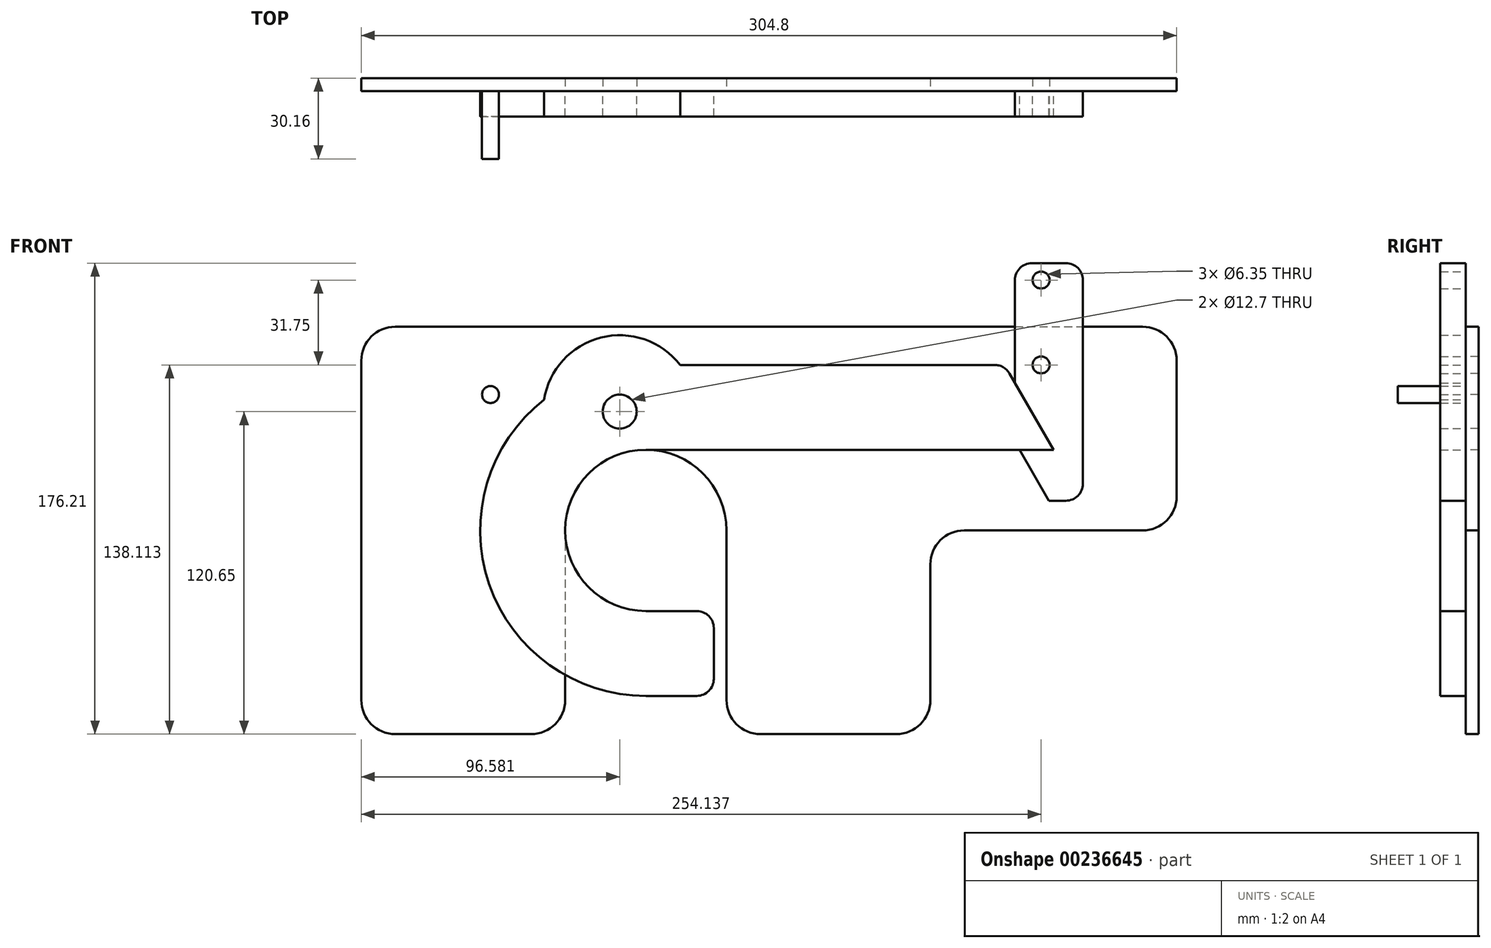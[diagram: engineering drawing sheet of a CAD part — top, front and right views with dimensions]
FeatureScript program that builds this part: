
annotation { "Feature Type Name" : "Feature", "Feature Type Description" : "" }
export const myFeature = defineFeature(function(context is Context, id is Id, definition is map)
    precondition{}
    {
        {
            var Q0;
            Q0=qCreatedBy(makeId("Front.planeOp"),FACE);
            var sketch = newSketch(context, id + "F0", { "sketchPlane" : qUnion([Q0])});
            skArc(sketch, "E0", {"start": v(0, 30.16) * mm, "mid": v(-30.16, 0) * mm, "end": v(0, -30.16) * mm});
            skLineSegment(sketch, "E1", {"start": v(19.05, -61.91) * mm, "end": v(0, -61.91) * mm});
            skLineSegment(sketch, "E2", {"start": v(0, 30.16) * mm, "end": v(152.4, 30.16) * mm});
            skLineSegment(sketch, "E3", {"start": v(0, -30.16) * mm, "end": v(19.05, -30.16) * mm});
            skLineSegment(sketch, "E4", {"start": v(25.4, -36.51) * mm, "end": v(25.4, -55.56) * mm});
            skCircle(sketch, "E5", {"center": v(-9.78, 44.45) * mm, "radius": 6.35 * mm});
            skArc(sketch, "E6", {"start": v(-38, 48.87) * mm, "mid": v(-58.56, -20.1) * mm, "end": v(0, -61.91) * mm});
            skLineSegment(sketch, "E7", {"start": v(12.84, 61.91) * mm, "end": v(130.4, 61.91) * mm});
            skLineSegment(sketch, "E8", {"start": v(152.4, 30.16) * mm, "end": v(135.9, 58.74) * mm});
            skArc(sketch, "E9", {"start": v(12.84, 61.91) * mm, "mid": v(-16.88, 72.13) * mm, "end": v(-38, 48.87) * mm});
            skPoint(sketch, "E10.visualSharp", {"position": v(25.4, -30.16) * mm});
            skArc(sketch, "E10.filletArc", {"start": v(25.4, -36.51) * mm, "mid": v(23.54, -32.02) * mm, "end": v(19.05, -30.16) * mm});
            skPoint(sketch, "E11.visualSharp", {"position": v(25.4, -61.91) * mm});
            skArc(sketch, "E11.filletArc", {"start": v(19.05, -61.91) * mm, "mid": v(23.54, -60.05) * mm, "end": v(25.4, -55.56) * mm});
            skPoint(sketch, "E12.visualSharp", {"position": v(134.07, 61.91) * mm});
            skArc(sketch, "E12.filletArc", {"start": v(135.9, 58.74) * mm, "mid": v(133.58, 61.06) * mm, "end": v(130.4, 61.91) * mm});
            skSolve(sketch);
        }
        {
            var Q0;
            Q0=qCreatedBy(makeId("Front.planeOp"),FACE);
            var sketch = newSketch(context, id + "F1", { "sketchPlane" : qUnion([Q0])});
            skLineSegment(sketch, "E13", {"start": v(152.4, 30.16) * mm, "end": v(139.7, 30.16) * mm});
            skLineSegment(sketch, "E14", {"start": v(139.7, 30.16) * mm, "end": v(150.7, 11.11) * mm});
            skLineSegment(sketch, "E15", {"start": v(150.7, 11.11) * mm, "end": v(157.05, 11.11) * mm});
            skLineSegment(sketch, "E16", {"start": v(163.4, 17.46) * mm, "end": v(163.4, 93.66) * mm});
            skLineSegment(sketch, "E17", {"start": v(157.05, 100.01) * mm, "end": v(144.35, 100.01) * mm});
            skLineSegment(sketch, "E18", {"start": v(138, 93.66) * mm, "end": v(138, 55.1) * mm});
            skCircle(sketch, "E19", {"center": v(147.78, 61.91) * mm, "radius": 3.18 * mm});
            skCircle(sketch, "E20", {"center": v(147.78, 93.66) * mm, "radius": 3.18 * mm});
            skLineSegment(sketch, "E21", {"start": v(152.4, 30.16) * mm, "end": v(138, 55.1) * mm});
            skPoint(sketch, "E22.visualSharp", {"position": v(163.4, 11.11) * mm});
            skArc(sketch, "E22.filletArc", {"start": v(157.05, 11.11) * mm, "mid": v(161.54, 12.97) * mm, "end": v(163.4, 17.46) * mm});
            skPoint(sketch, "E23.visualSharp", {"position": v(163.4, 100.01) * mm});
            skArc(sketch, "E23.filletArc", {"start": v(163.4, 93.66) * mm, "mid": v(161.54, 98.15) * mm, "end": v(157.05, 100.01) * mm});
            skPoint(sketch, "E24.visualSharp", {"position": v(138, 100.01) * mm});
            skArc(sketch, "E24.filletArc", {"start": v(144.35, 100.01) * mm, "mid": v(139.86, 98.15) * mm, "end": v(138, 93.66) * mm});
            skSolve(sketch);
        }
        {
            var Q0;
            Q0=makeQuery(id+"F0.imprint","IMPRINT",FACE,{"disambiguationData":[TD([[makeQuery(id+"F0.imprint","IMPRINT",EDGE,{"derivedFrom":sQuery(id+"F0.wireOp",EDGE,"E0")}),-1.0]])]});
            var Q1;
            Q1=makeQuery(id+"F1.imprint","IMPRINT",FACE,{"disambiguationData":[TD([[makeQuery(id+"F1.imprint","IMPRINT",EDGE,{"derivedFrom":sQuery(id+"F1.wireOp",EDGE,"E13")}),1.0]])]});
            extrude(context, id + "F2", {"entities" : qUnion([Q0, Q1]), "depth" : 9.52 * mm});
        }
        {
            var Q0;
            Q0=qCreatedBy(makeId("Front.planeOp"),FACE);
            var sketch = newSketch(context, id + "F3", { "sketchPlane" : qUnion([Q0])});
            skCircle(sketch, "E25", {"center": v(-58.06, 50.83) * mm, "radius": 3.18 * mm});
            skSolve(sketch);
        }
        {
            var Q0;
            Q0=makeQuery(id+"F3.imprint","IMPRINT",FACE,{"disambiguationData":[TD([[makeQuery(id+"F3.imprint","IMPRINT",EDGE,{"derivedFrom":sQuery(id+"F3.wireOp",EDGE,"E25")}),1.0]])]});
            extrude(context, id + "F4", {"entities" : qUnion([Q0]), "depth" : 25.4 * mm});
        }
        {
            var Q0;
            Q0=makeQuery(id+"F0.imprint","IMPRINT",FACE,{"disambiguationData":[TD([[makeQuery(id+"F0.imprint","IMPRINT",EDGE,{"derivedFrom":sQuery(id+"F0.wireOp",EDGE,"E0")}),-1.0]])]});
            var sketch = newSketch(context, id + "F5", { "sketchPlane" : qUnion([Q0])});
            skArc(sketch, "E26", {"start": v(30.16, 0) * mm, "mid": v(0, 30.16) * mm, "end": v(-30.16, 0) * mm});
            skCircle(sketch, "E27.0", {"center": v(-9.78, 44.45) * mm, "radius": 6.35 * mm});
            skCircle(sketch, "E28.0", {"center": v(147.78, 61.91) * mm, "radius": 3.18 * mm});
            skLineSegment(sketch, "E29", {"start": v(30.16, 0) * mm, "end": v(30.16, -63.5) * mm});
            skLineSegment(sketch, "E30", {"start": v(-30.16, 0) * mm, "end": v(-30.16, -63.5) * mm});
            skLineSegment(sketch, "E31", {"start": v(-42.86, -76.2) * mm, "end": v(-93.66, -76.2) * mm});
            skLineSegment(sketch, "E32", {"start": v(-106.36, -63.5) * mm, "end": v(-106.36, 63.5) * mm});
            skLineSegment(sketch, "E33", {"start": v(-93.66, 76.2) * mm, "end": v(185.74, 76.2) * mm});
            skLineSegment(sketch, "E34", {"start": v(198.44, 63.5) * mm, "end": v(198.44, 12.7) * mm});
            skLineSegment(sketch, "E35", {"start": v(93.66, -76.2) * mm, "end": v(42.86, -76.2) * mm});
            skLineSegment(sketch, "E36", {"start": v(106.36, -63.5) * mm, "end": v(106.36, -12.7) * mm});
            skLineSegment(sketch, "E37", {"start": v(119.06, 0) * mm, "end": v(185.74, 0) * mm});
            skPoint(sketch, "E38.visualSharp", {"position": v(-106.36, 76.2) * mm});
            skArc(sketch, "E38.filletArc", {"start": v(-93.66, 76.2) * mm, "mid": v(-102.64, 72.48) * mm, "end": v(-106.36, 63.5) * mm});
            skPoint(sketch, "E39.visualSharp", {"position": v(-106.36, -76.2) * mm});
            skArc(sketch, "E39.filletArc", {"start": v(-106.36, -63.5) * mm, "mid": v(-102.64, -72.48) * mm, "end": v(-93.66, -76.2) * mm});
            skPoint(sketch, "E40.visualSharp", {"position": v(-30.16, -76.2) * mm});
            skArc(sketch, "E40.filletArc", {"start": v(-42.86, -76.2) * mm, "mid": v(-33.88, -72.48) * mm, "end": v(-30.16, -63.5) * mm});
            skPoint(sketch, "E41.visualSharp", {"position": v(30.16, -76.2) * mm});
            skArc(sketch, "E41.filletArc", {"start": v(30.16, -63.5) * mm, "mid": v(33.88, -72.48) * mm, "end": v(42.86, -76.2) * mm});
            skPoint(sketch, "E42.visualSharp", {"position": v(106.36, -76.2) * mm});
            skArc(sketch, "E42.filletArc", {"start": v(93.66, -76.2) * mm, "mid": v(102.64, -72.48) * mm, "end": v(106.36, -63.5) * mm});
            skPoint(sketch, "E43.visualSharp", {"position": v(106.36, 0) * mm});
            skArc(sketch, "E43.filletArc", {"start": v(119.06, 0) * mm, "mid": v(110.08, -3.72) * mm, "end": v(106.36, -12.7) * mm});
            skPoint(sketch, "E44.visualSharp", {"position": v(198.44, 0) * mm});
            skArc(sketch, "E44.filletArc", {"start": v(185.74, 0) * mm, "mid": v(194.72, 3.72) * mm, "end": v(198.44, 12.7) * mm});
            skPoint(sketch, "E45.visualSharp", {"position": v(198.44, 76.2) * mm});
            skArc(sketch, "E45.filletArc", {"start": v(198.44, 63.5) * mm, "mid": v(194.72, 72.48) * mm, "end": v(185.74, 76.2) * mm});
            skSolve(sketch);
        }
        {
            var Q0;
            Q0=makeQuery(id+"F5.imprint","IMPRINT",FACE,{"disambiguationData":[TD([[makeQuery(id+"F5.imprint","IMPRINT",EDGE,{"derivedFrom":sQuery(id+"F5.wireOp",EDGE,"E28.0")}),-1.0]])]});
            var Q1;
            Q1=makeQuery(id+"F5.imprint","IMPRINT",FACE,{"disambiguationData":[TD([[makeQuery(id+"F5.imprint","IMPRINT",EDGE,{"derivedFrom":sQuery(id+"F5.wireOp",EDGE,"E27.0")}),-1.0]])]});
            extrude(context, id + "F6", {"entities" : qUnion([Q0, Q1]), "oppositeDirection" : true, "depth" : 4.76 * mm});
        }
    });
